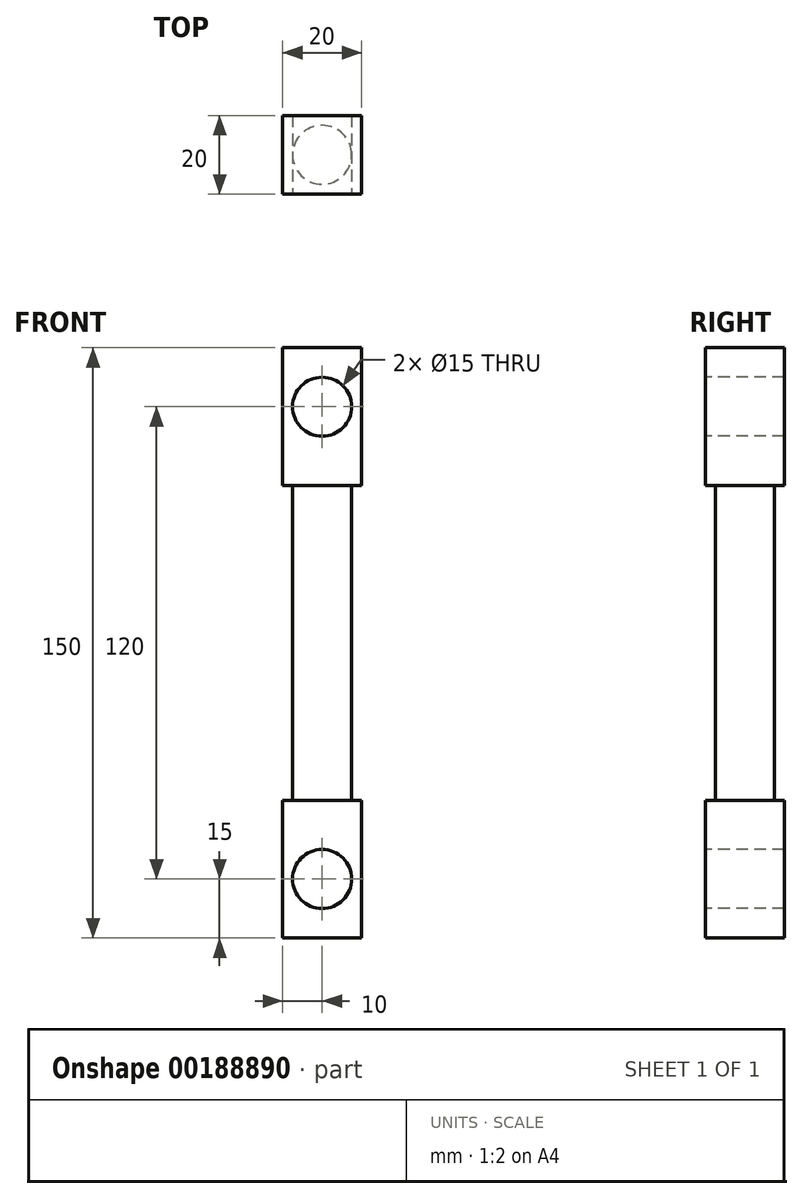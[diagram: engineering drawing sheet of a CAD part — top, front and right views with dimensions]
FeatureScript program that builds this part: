
annotation { "Feature Type Name" : "Feature", "Feature Type Description" : "" }
export const myFeature = defineFeature(function(context is Context, id is Id, definition is map)
    precondition{}
    {
        {
            var Q0;
            Q0=qCreatedBy(makeId("Top.planeOp"),FACE);
            var sketch = newSketch(context, id + "F0", { "sketchPlane" : qUnion([Q0])});
            skCircle(sketch, "E0", {"center": v(0, 0) * mm, "radius": 7.5 * mm});
            skSolve(sketch);
        }
        {
            var Q0;
            Q0=qSketchRegion(id+"F0",true);
            extrude(context, id + "F1", {"entities" : qUnion([Q0]), "depth" : 150 * mm});
        }
        {
            var Q0;
            Q0=qCreatedBy(makeId("Top.planeOp"),FACE);
            cPlane(context, id + "F2", {"entities" : qUnion([Q0]), "cplaneType" : CPlaneType.OFFSET, "offset" : 35 * mm, "width" : 150 * mm, "height" : 150 * mm});
        }
        {
            var Q0;
            Q0=qCreatedBy(makeId("Top.planeOp"),FACE);
            cPlane(context, id + "F3", {"entities" : qUnion([Q0]), "cplaneType" : CPlaneType.OFFSET, "offset" : 115 * mm, "width" : 150 * mm, "height" : 150 * mm});
        }
        {
            var Q0;
            Q0=qCreatedBy(id+"F2.planeOp",FACE);
            var sketch = newSketch(context, id + "F4", { "sketchPlane" : qUnion([Q0])});
            skLineSegment(sketch, "E1.bottom", {"start": v(10, -10) * mm, "end": v(-10, -10) * mm});
            skLineSegment(sketch, "E1.top", {"start": v(10, 10) * mm, "end": v(-10, 10) * mm});
            skLineSegment(sketch, "E1.left", {"start": v(10, -10) * mm, "end": v(10, 10) * mm});
            skLineSegment(sketch, "E1.right", {"start": v(-10, -10) * mm, "end": v(-10, 10) * mm});
            skPoint(sketch, "E1.middle", {"position": v(0, 0) * mm});
            skSolve(sketch);
        }
        {
            var Q0;
            Q0=qSketchRegion(id+"F4",true);
            extrude(context, id + "F5", {"entities" : qUnion([Q0]), "operationType" : NewBodyOperationType.ADD, "oppositeDirection" : true, "depth" : 35 * mm});
        }
        {
            var Q0;
            Q0=qCreatedBy(id+"F3.planeOp",FACE);
            var sketch = newSketch(context, id + "F6", { "sketchPlane" : qUnion([Q0])});
            skLineSegment(sketch, "E2.bottom", {"start": v(10, -10) * mm, "end": v(-10, -10) * mm});
            skLineSegment(sketch, "E2.top", {"start": v(10, 10) * mm, "end": v(-10, 10) * mm});
            skLineSegment(sketch, "E2.left", {"start": v(10, -10) * mm, "end": v(10, 10) * mm});
            skLineSegment(sketch, "E2.right", {"start": v(-10, -10) * mm, "end": v(-10, 10) * mm});
            skPoint(sketch, "E2.middle", {"position": v(0, 0) * mm});
            skSolve(sketch);
        }
        {
            var Q0;
            Q0=qSketchRegion(id+"F6",true);
            extrude(context, id + "F7", {"entities" : qUnion([Q0]), "operationType" : NewBodyOperationType.ADD, "depth" : 35 * mm});
        }
        {
            var Q0;
            Q0=makeQuery(id+"F7.opExtrude","SWEPT_FACE",FACE,{"disambiguationData":[OSD([sQuery(id+"F6.wireOp",EDGE,"E2.bottom")])]});
            var sketch = newSketch(context, id + "F8", { "sketchPlane" : qUnion([Q0])});
            skCircle(sketch, "E3", {"center": v(0, 135) * mm, "radius": 7.5 * mm});
            skCircle(sketch, "E4", {"center": v(0, 15) * mm, "radius": 7.5 * mm});
            skSolve(sketch);
        }
        {
            var Q0;
            Q0=qSketchRegion(id+"F8",true);
            extrude(context, id + "F9", {"entities" : qUnion([Q0]), "operationType" : NewBodyOperationType.REMOVE, "endBound" : BoundingType.UP_TO_NEXT, "oppositeDirection" : true, "depth" : 25 * mm});
        }
    });
